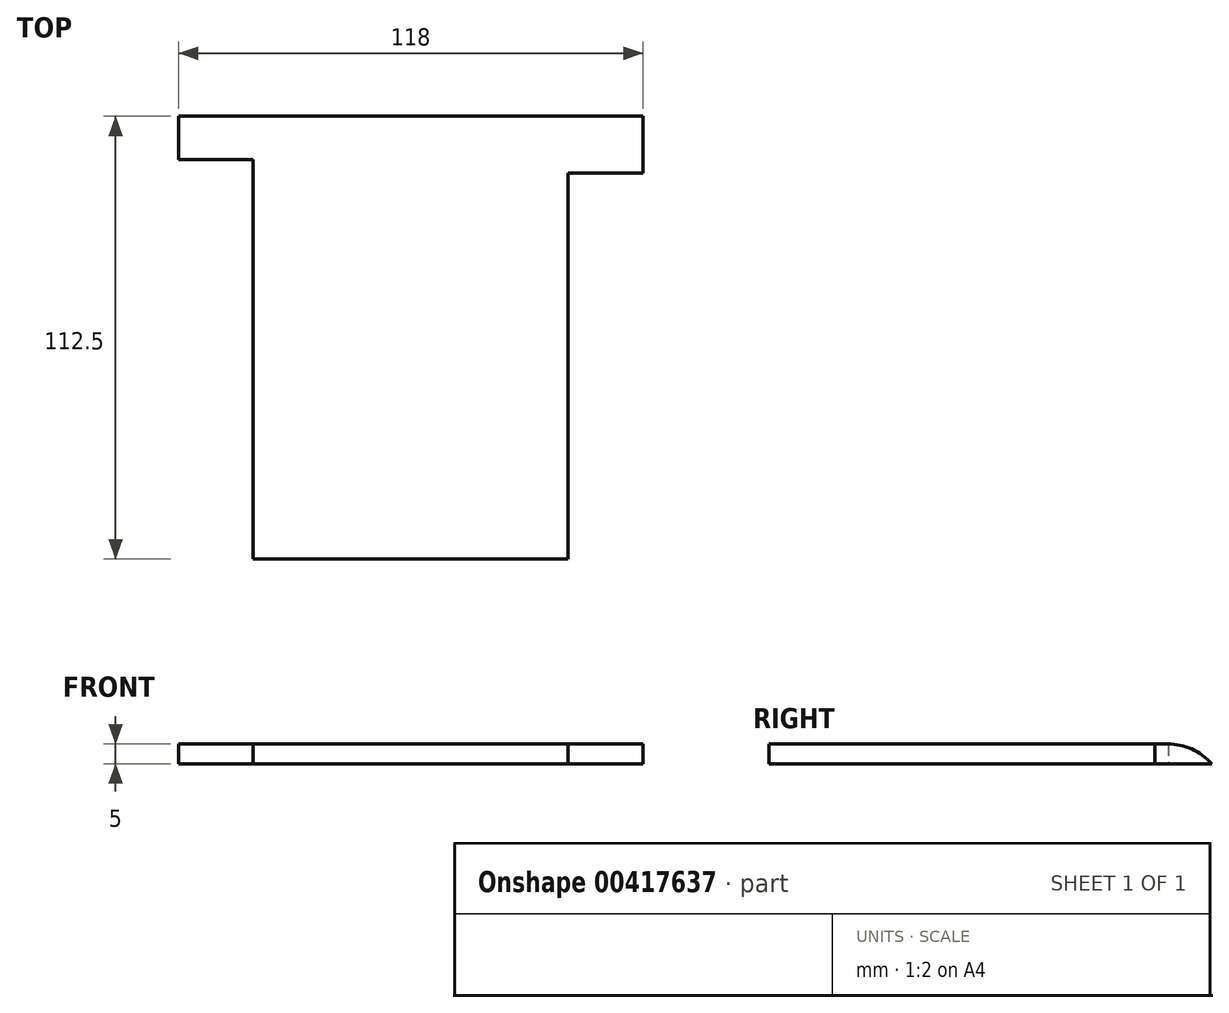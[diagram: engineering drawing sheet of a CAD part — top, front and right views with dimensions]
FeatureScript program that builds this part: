
annotation { "Feature Type Name" : "Feature", "Feature Type Description" : "" }
export const myFeature = defineFeature(function(context is Context, id is Id, definition is map)
    precondition{}
    {
        {
            assignVariable(context, id + "F0", {"name" : "Thickness", "anyValue" : 5});
        }
        {
            var Q0;
            Q0=qCreatedBy(makeId("Top.planeOp"),FACE);
            var sketch = newSketch(context, id + "F1", { "sketchPlane" : qUnion([Q0])});
            skLineSegment(sketch, "E0.bottom", {"start": v(40.37, -56.17) * mm, "end": v(-39.63, -56.17) * mm});
            skLineSegment(sketch, "E0.left", {"start": v(40.37, -56.17) * mm, "end": v(40.37, 41.83) * mm});
            skLineSegment(sketch, "E0.right", {"start": v(-39.63, -56.17) * mm, "end": v(-39.63, 45.33) * mm});
            skPoint(sketch, "E0.middle", {"position": v(0, 0) * mm});
            skLineSegment(sketch, "E1", {"start": v(-39.63, 45.33) * mm, "end": v(-58.63, 45.33) * mm});
            skLineSegment(sketch, "E2", {"start": v(40.37, 41.83) * mm, "end": v(59.37, 41.83) * mm});
            skLineSegment(sketch, "E3", {"start": v(59.37, 41.83) * mm, "end": v(59.37, 56.33) * mm});
            skLineSegment(sketch, "E4", {"start": v(59.37, 56.33) * mm, "end": v(-58.63, 56.33) * mm});
            skLineSegment(sketch, "E5", {"start": v(-58.63, 56.33) * mm, "end": v(-58.63, 45.33) * mm});
            skLineSegment(sketch, "E6", {"start": v(0, -56.17) * mm, "end": v(0.37, 78.2) * mm, "construction": true});
            skPoint(sketch, "E6.startSnap0", {"position": v(0.37, -56.17) * mm});
            skPoint(sketch, "E6.endSnap0", {"position": v(0.37, -56.17) * mm});
            skSolve(sketch);
        }
        {
            var Q0;
            Q0=makeQuery(id+"F1.imprint","IMPRINT",FACE,{"disambiguationData":[TD([[makeQuery(id+"F1.imprint","IMPRINT",EDGE,{"derivedFrom":sQuery(id+"F1.wireOp",EDGE,"E0.bottom")}),-1.0]])]});
            extrude(context, id + "F2", {"entities" : qUnion([Q0]), "depth" : (getVariable(context, 'Thickness')) * mm});
        }
        {
            var Q0;
            Q0=makeQuery(id+"F2.opExtrude","CAP_EDGE",EDGE,{"disambiguationData":[OSD([sQuery(id+"F1.wireOp",EDGE,"E4")])],"isStart":false});
            fillet(context, id + "F3", {"entities" : qUnion([Q0]), "radius" : 15 * mm, "allowEdgeOverflow" : false});
        }
    });
